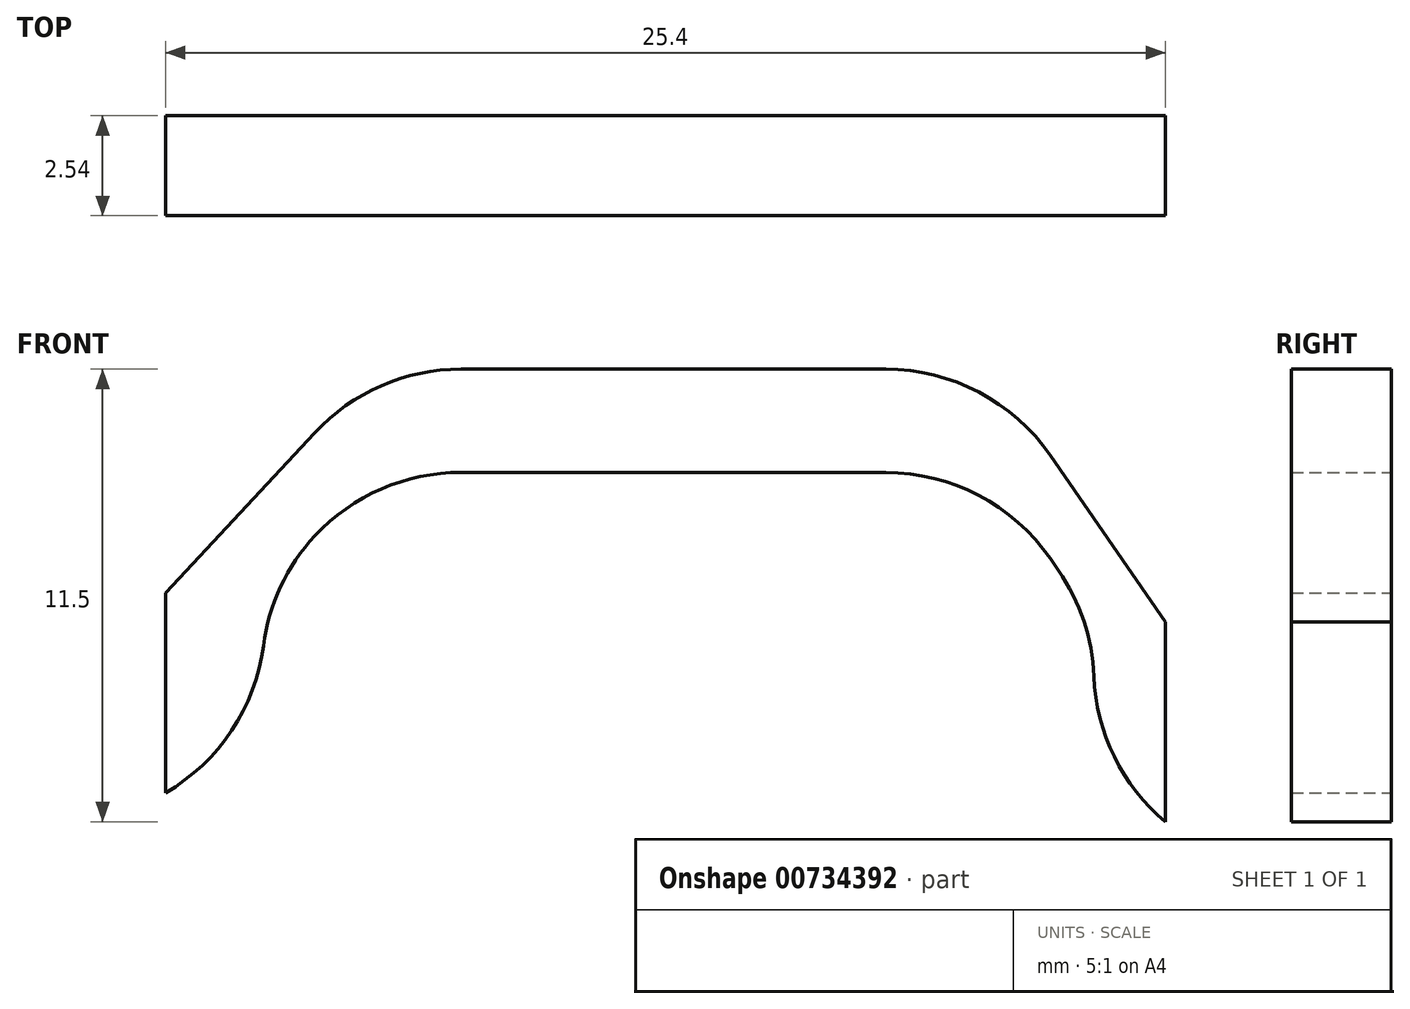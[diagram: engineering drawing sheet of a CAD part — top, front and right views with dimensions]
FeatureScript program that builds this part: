
annotation { "Feature Type Name" : "Feature", "Feature Type Description" : "" }
export const myFeature = defineFeature(function(context is Context, id is Id, definition is map)
    precondition{}
    {
        {
            var Q0;
            Q0=qCreatedBy(makeId("Front.planeOp"),FACE);
            var sketch = newSketch(context, id + "F0", { "sketchPlane" : qUnion([Q0])});
            skLineSegment(sketch, "E0", {"start": v(-36.75, -5.68) * mm, "end": v(-36.75, -10.76) * mm});
            skLineSegment(sketch, "E1", {"start": v(-11.35, -6.42) * mm, "end": v(-11.35, -11.5) * mm});
            skLineSegment(sketch, "E2", {"start": v(-36.75, -5.68) * mm, "end": v(-31.46, 0) * mm});
            skLineSegment(sketch, "E3", {"start": v(-11.35, -6.42) * mm, "end": v(-15.79, 0) * mm});
            skLineSegment(sketch, "E4", {"start": v(-15.79, 0) * mm, "end": v(-31.46, 0) * mm});
            skLineSegment(sketch, "E5", {"start": v(-36.75, -10.76) * mm, "end": v(-34.3, -10.76) * mm});
            skLineSegment(sketch, "E6", {"start": v(-15.79, -2.62) * mm, "end": v(-13.16, -6.42) * mm});
            skLineSegment(sketch, "E7", {"start": v(-13.16, -6.42) * mm, "end": v(-13.16, -11.5) * mm});
            skLineSegment(sketch, "E8", {"start": v(-13.16, -11.5) * mm, "end": v(-11.35, -11.5) * mm});
            skLineSegment(sketch, "E9", {"start": v(-34.3, -10.76) * mm, "end": v(-34.3, -5.68) * mm});
            skLineSegment(sketch, "E10", {"start": v(-34.3, -5.68) * mm, "end": v(-31.46, -2.62) * mm});
            skLineSegment(sketch, "E11", {"start": v(-31.46, -2.62) * mm, "end": v(-15.79, -2.62) * mm});
            skSolve(sketch);
        }
        {
            var Q0;
            Q0=makeQuery(id+"F0.imprint","IMPRINT",FACE,{"disambiguationData":[TD([[makeQuery(id+"F0.imprint","IMPRINT",EDGE,{"derivedFrom":sQuery(id+"F0.wireOp",EDGE,"E0")}),1.0]])]});
            extrude(context, id + "F1", {"entities" : qUnion([Q0]), "depth" : 2.54 * mm, "offsetDistance" : 25.4 * mm});
        }
        {
            var Q0;
            Q0=makeQuery(id+"F1.opExtrude","SWEPT_EDGE",EDGE,{"disambiguationData":[OSD([sQuery(id+"F0.wireOp",EDGE,"E10"),sQuery(id+"F0.wireOp",EDGE,"E11")])]});
            var Q1;
            Q1=makeQuery(id+"F1.opExtrude","SWEPT_EDGE",EDGE,{"disambiguationData":[OSD([sQuery(id+"F0.wireOp",EDGE,"E6"),sQuery(id+"F0.wireOp",EDGE,"E11")])]});
            var Q2;
            Q2=makeQuery(id+"F1.opExtrude","SWEPT_EDGE",EDGE,{"disambiguationData":[OSD([sQuery(id+"F0.wireOp",EDGE,"E6"),sQuery(id+"F0.wireOp",EDGE,"E7")])]});
            var Q3;
            Q3=makeQuery(id+"F1.opExtrude","SWEPT_EDGE",EDGE,{"disambiguationData":[OSD([sQuery(id+"F0.wireOp",EDGE,"E9"),sQuery(id+"F0.wireOp",EDGE,"E10")])]});
            var Q4;
            Q4=makeQuery(id+"F1.opExtrude","SWEPT_EDGE",EDGE,{"disambiguationData":[OSD([sQuery(id+"F0.wireOp",EDGE,"E2"),sQuery(id+"F0.wireOp",EDGE,"E4")])]});
            var Q5;
            Q5=makeQuery(id+"F1.opExtrude","SWEPT_EDGE",EDGE,{"disambiguationData":[OSD([sQuery(id+"F0.wireOp",EDGE,"E3"),sQuery(id+"F0.wireOp",EDGE,"E4")])]});
            fillet(context, id + "F2", {"entities" : qUnion([Q0, Q1, Q2, Q3, Q4, Q5]), "radius" : 5.08 * mm, "tangentPropagation" : true, "allowEdgeOverflow" : false});
        }
        {
            var Q0;
            Q0=makeQuery(id+"F1.opExtrude","SWEPT_EDGE",EDGE,{"disambiguationData":[OSD([sQuery(id+"F0.wireOp",EDGE,"E7"),sQuery(id+"F0.wireOp",EDGE,"E8")])]});
            var Q1;
            Q1=makeQuery(id+"F1.opExtrude","SWEPT_EDGE",EDGE,{"disambiguationData":[OSD([sQuery(id+"F0.wireOp",EDGE,"E5"),sQuery(id+"F0.wireOp",EDGE,"E9")])]});
            fillet(context, id + "F3", {"entities" : qUnion([Q0, Q1]), "radius" : 5.08 * mm, "tangentPropagation" : true, "allowEdgeOverflow" : false});
        }
    });
